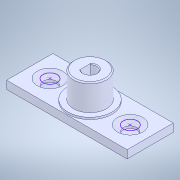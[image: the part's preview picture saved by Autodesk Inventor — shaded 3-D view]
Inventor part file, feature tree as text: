
AUTODESK INVENTOR PART (.ipt)
format: ipt  version: 2021 (Build 250183000, 183)  size: 171,008 bytes
history: native  units: in
note: dims shown in document units (in); Inventor stores cm internally (conversion verified against a paired STEP export)
features: sketch x5, extrude x4, chamfer x2, projected_geometry x2, hole x1, other x1
ambient origin geometry x8: Origin, YZ Plane, XZ Plane, XY Plane, X Axis, Y Axis, Z Axis, Center Point
bodies: Solid1 (feature_tree)
feature tree (15):
  extrude  "Extrusion1"  Depth=0.3937in TaperAngle=0.0deg
  extrude  "Extrusion2"  Depth=0.3937in TaperAngle=0.0deg
  extrude  "Extrusion3"  Depth=0.002in
  extrude  "Extrusion4"  Depth=0.3937in TaperAngle=45.0deg
  chamfer  "Chamfer1"  Distance=0.3937in
  hole  "Hole2"  [1 undecoded]
  chamfer  "Chamfer2"  [1 undecoded]
  sketch  "Sketch1"  dims[d1=0.3937in d2=0.0in d3=0.3937in d4=0.0in]
  projected_geometry  "Projected Loop1"
  sketch  "Sketch2"  dims[d5=0.0039in d6=0.3937in d7=0.0in]
  sketch  "Sketch3"  dims[d8=0.0118in d9=0.0787in d10=45.0deg]
  sketch  "Sketch6"  dims[d19=0.1339in d20=0.2362in d21=0.248in d22=0.0787in d23=90.0deg d24=0.315in d25=0.0in d26=0.002in]
  sketch  "Sketch7"  dims[d27=0.002in d28=0.0079in d29=0.0787in d30=45.0deg d32=0.3937in d33=0.0in d34=0.0039in]
  projected_geometry  "Projected Loop2"
  other  "CSK for M4 Countersunk Flat Head Screw1"
note: 2 required parameter values undecoded (feature->parameter linkage not recoverable at this tier; creation-order binding heuristic only, values carry confidence <= 0.55)
